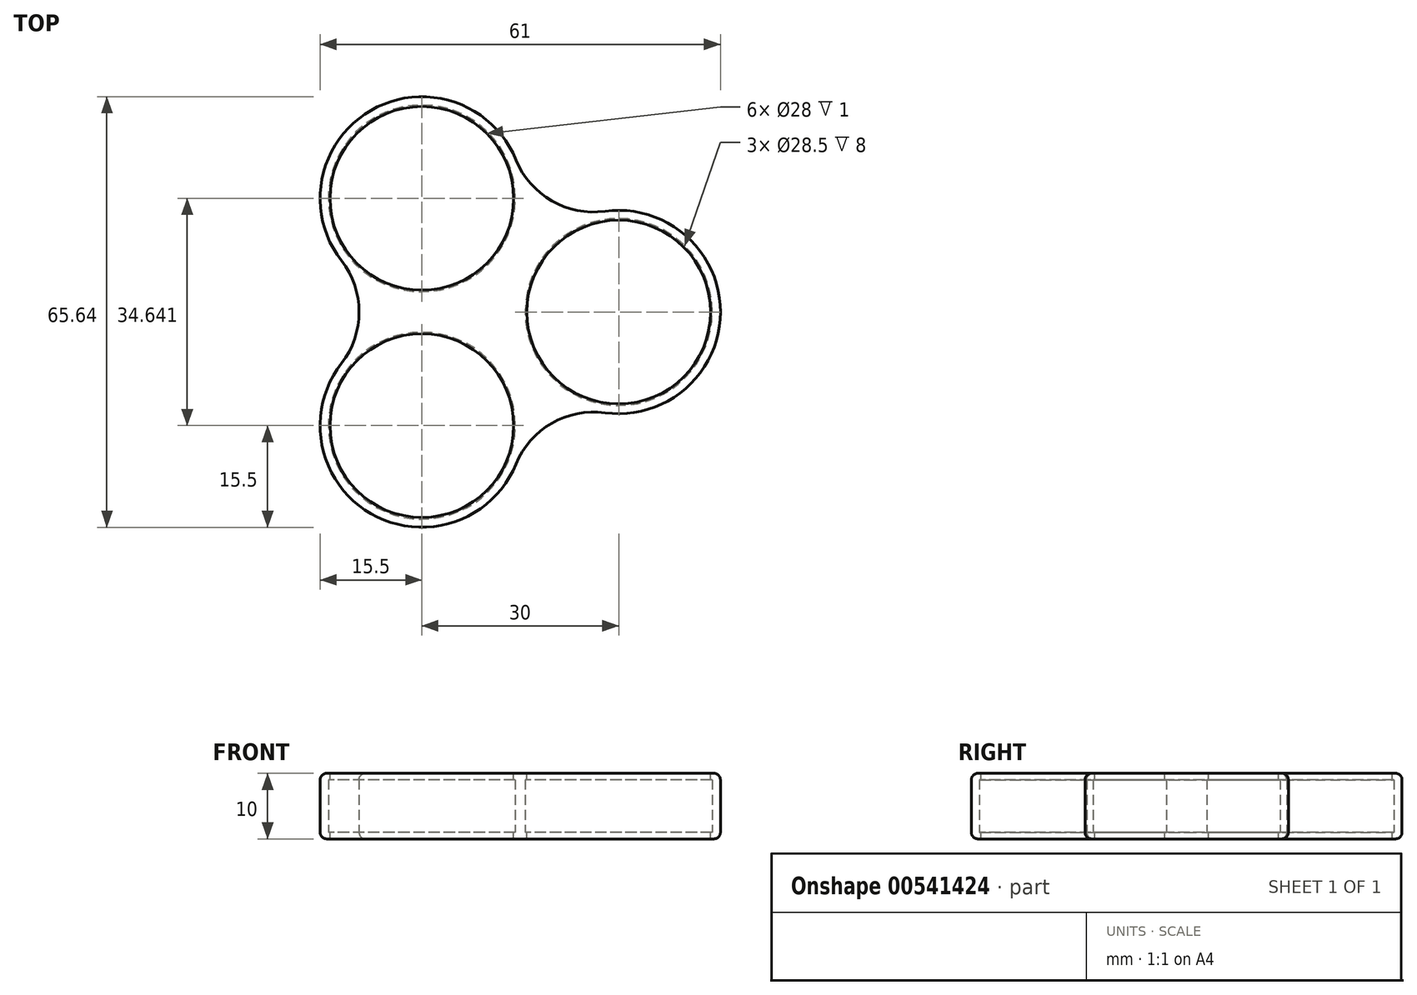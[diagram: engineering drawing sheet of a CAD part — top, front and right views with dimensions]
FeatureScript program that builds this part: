
annotation { "Feature Type Name" : "Feature", "Feature Type Description" : "" }
export const myFeature = defineFeature(function(context is Context, id is Id, definition is map)
    precondition{}
    {
        {
            var Q0;
            Q0=qCreatedBy(makeId("Top.planeOp"),FACE);
            var sketch = newSketch(context, id + "F0", { "sketchPlane" : qUnion([Q0])});
            skCircle(sketch, "E0", {"center": v(20, 0) * mm, "radius": 15.5 * mm});
            skCircle(sketch, "E1.1.0", {"center": v(-10, 17.32) * mm, "radius": 15.5 * mm});
            skCircle(sketch, "E1.2.0", {"center": v(-10, -17.32) * mm, "radius": 15.5 * mm});
            skPoint(sketch, "E1.center", {"position": v(0, 0) * mm});
            skCircle(sketch, "E2", {"center": v(16.18, 28.03) * mm, "radius": 12.79 * mm});
            skCircle(sketch, "E3.1.0", {"center": v(-32.36, 0) * mm, "radius": 12.79 * mm});
            skCircle(sketch, "E3.2.0", {"center": v(16.18, -28.03) * mm, "radius": 12.79 * mm});
            skSolve(sketch);
        }
        {
            var Q0;
            {var subQ0=sQuery(id+"F0.wireOp",EDGE,"E2");var subQ1=sQuery(id+"F0.wireOp",EDGE,"E0");var subQ2=makeQuery(id+"F0.imprint","INTERSECT",VERTEX,{"disambiguationData":[OD(0.0)],"derivedFrom":[subQ1,subQ0]});Q0=makeQuery(id+"F0.imprint","IMPRINT",FACE,{"disambiguationData":[TD([[makeQuery(id+"F0.imprint","IMPRINT",EDGE,{"disambiguationData":[TD([[subQ2,-1.0]])],"derivedFrom":subQ1}),1.0]])]});}
            var Q1;
            {var subQ0=sQuery(id+"F0.wireOp",EDGE,"E0");var subQ1=makeQuery(id+"F0.imprint","INTERSECT",VERTEX,{"derivedFrom":[subQ0,sQuery(id+"F0.wireOp",EDGE,"E3.2.0")]});Q1=makeQuery(id+"F0.imprint","IMPRINT",FACE,{"disambiguationData":[TD([[makeQuery(id+"F0.imprint","IMPRINT",EDGE,{"disambiguationData":[TD([[subQ1,1.0]])],"derivedFrom":subQ0}),1.0]])]});}
            var Q2;
            {var subQ0=sQuery(id+"F0.wireOp",EDGE,"E3.1.0");var subQ1=sQuery(id+"F0.wireOp",EDGE,"E1.1.0");var subQ2=makeQuery(id+"F0.imprint","INTERSECT",VERTEX,{"disambiguationData":[OD(0.0)],"derivedFrom":[subQ1,subQ0]});Q2=makeQuery(id+"F0.imprint","IMPRINT",FACE,{"disambiguationData":[TD([[makeQuery(id+"F0.imprint","IMPRINT",EDGE,{"disambiguationData":[TD([[subQ2,-1.0]])],"derivedFrom":subQ1}),1.0]])]});}
            var Q3;
            {var subQ0=sQuery(id+"F0.wireOp",EDGE,"E3.2.0");var subQ1=sQuery(id+"F0.wireOp",EDGE,"E1.2.0");var subQ2=makeQuery(id+"F0.imprint","INTERSECT",VERTEX,{"disambiguationData":[OD(0.0)],"derivedFrom":[subQ1,subQ0]});Q3=makeQuery(id+"F0.imprint","IMPRINT",FACE,{"disambiguationData":[TD([[makeQuery(id+"F0.imprint","IMPRINT",EDGE,{"disambiguationData":[TD([[subQ2,-1.0]])],"derivedFrom":subQ1}),1.0]])]});}
            var Q4;
            {var subQ0=sQuery(id+"F0.wireOp",EDGE,"E1.2.0");var subQ1=makeQuery(id+"F0.imprint","INTERSECT",VERTEX,{"derivedFrom":[subQ0,sQuery(id+"F0.wireOp",EDGE,"E3.1.0")]});Q4=makeQuery(id+"F0.imprint","IMPRINT",FACE,{"disambiguationData":[TD([[makeQuery(id+"F0.imprint","IMPRINT",EDGE,{"disambiguationData":[TD([[subQ1,1.0]])],"derivedFrom":subQ0}),1.0]])]});}
            var Q5;
            {var subQ3=sQuery(id+"F0.wireOp",EDGE,"E3.2.0");var subQ8=sQuery(id+"F0.wireOp",EDGE,"E0");var subQ11=makeQuery(id+"F0.imprint","INTERSECT",VERTEX,{"derivedFrom":[subQ8,subQ3]});Q5=makeQuery(id+"F0.imprint","IMPRINT",FACE,{"disambiguationData":[TD([[makeQuery(id+"F0.imprint","IMPRINT",EDGE,{"disambiguationData":[TD([[subQ11,1.0]])],"derivedFrom":subQ8}),-1.0]])]});}
            var Q6;
            {var subQ0=sQuery(id+"F0.wireOp",EDGE,"E1.1.0");var subQ1=makeQuery(id+"F0.imprint","INTERSECT",VERTEX,{"derivedFrom":[subQ0,sQuery(id+"F0.wireOp",EDGE,"E2")]});Q6=makeQuery(id+"F0.imprint","IMPRINT",FACE,{"disambiguationData":[TD([[makeQuery(id+"F0.imprint","IMPRINT",EDGE,{"disambiguationData":[TD([[subQ1,1.0]])],"derivedFrom":subQ0}),1.0]])]});}
            extrude(context, id + "F1", {"entities" : qUnion([Q0, Q1, Q2, Q3, Q4, Q5, Q6]), "depth" : 10 * mm, "offsetDistance" : 25 * mm});
        }
        {
            var Q0;
            Q0=qCreatedBy(makeId("Top.planeOp"),FACE);
            var sketch = newSketch(context, id + "F2", { "sketchPlane" : qUnion([Q0])});
            skCircle(sketch, "E4", {"center": v(20, 0) * mm, "radius": 14 * mm});
            skCircle(sketch, "E5.1.0", {"center": v(-10, 17.32) * mm, "radius": 14 * mm});
            skCircle(sketch, "E5.2.0", {"center": v(-10, -17.32) * mm, "radius": 14 * mm});
            skPoint(sketch, "E5.center", {"position": v(0, 0) * mm});
            skSolve(sketch);
        }
        {
            var Q0;
            Q0 = qSketchRegion(id + "F2", true);
            extrude(context, id + "F3", {"entities" : qUnion([Q0]), "operationType" : NewBodyOperationType.REMOVE, "oppositeDirection" : true, "depth" : 25 * mm, "offsetDistance" : 25 * mm, "hasSecondDirection" : true, "secondDirectionOppositeDirection" : true, "secondDirectionDepth" : -25 * mm});
        }
        {
            var Q0;
            Q0=qCreatedBy(makeId("Top.planeOp"),FACE);
            var sketch = newSketch(context, id + "F4", { "sketchPlane" : qUnion([Q0])});
            skCircle(sketch, "E6", {"center": v(20, 0) * mm, "radius": 14.25 * mm});
            skCircle(sketch, "E7.1.0", {"center": v(-10, 17.32) * mm, "radius": 14.25 * mm});
            skCircle(sketch, "E7.2.0", {"center": v(-10, -17.32) * mm, "radius": 14.25 * mm});
            skPoint(sketch, "E7.center", {"position": v(0, 0) * mm});
            skSolve(sketch);
        }
        {
            var Q0;
            Q0 = qSketchRegion(id + "F4", true);
            extrude(context, id + "F5", {"entities" : qUnion([Q0]), "operationType" : NewBodyOperationType.REMOVE, "depth" : 9 * mm, "offsetDistance" : 25 * mm, "hasSecondDirection" : true, "secondDirectionOppositeDirection" : true, "secondDirectionDepth" : -1 * mm});
        }
        {
            var Q0;
            Q0=makeQuery(id+"F1.opExtrude","CAP_EDGE",EDGE,{"disambiguationData":[OSD([sQuery(id+"F0.wireOp",EDGE,"E1.2.0")])],"isStart":false});
            var Q1;
            Q1=makeQuery(id+"F1.opExtrude","CAP_EDGE",EDGE,{"disambiguationData":[OSD([sQuery(id+"F0.wireOp",EDGE,"E3.2.0")])],"isStart":false});
            var Q2;
            Q2=makeQuery(id+"F1.opExtrude","CAP_EDGE",EDGE,{"disambiguationData":[OSD([sQuery(id+"F0.wireOp",EDGE,"E0")])],"isStart":false});
            var Q3;
            Q3=makeQuery(id+"F1.opExtrude","CAP_EDGE",EDGE,{"disambiguationData":[OSD([sQuery(id+"F0.wireOp",EDGE,"E2")])],"isStart":false});
            var Q4;
            Q4=makeQuery(id+"F1.opExtrude","CAP_EDGE",EDGE,{"disambiguationData":[OSD([sQuery(id+"F0.wireOp",EDGE,"E3.1.0")])],"isStart":false});
            var Q5;
            Q5=makeQuery(id+"F1.opExtrude","CAP_EDGE",EDGE,{"disambiguationData":[OSD([sQuery(id+"F0.wireOp",EDGE,"E1.1.0")])],"isStart":false});
            fillet(context, id + "F6", {"entities" : qUnion([Q0, Q1, Q2, Q3, Q4, Q5]), "radius" : 1 * mm, "tangentPropagation" : true, "allowEdgeOverflow" : false});
        }
        {
            var Q0;
            Q0=makeQuery(id+"F1.opExtrude","CAP_EDGE",EDGE,{"disambiguationData":[OSD([sQuery(id+"F0.wireOp",EDGE,"E1.1.0")])],"isStart":true});
            var Q1;
            Q1=makeQuery(id+"F1.opExtrude","CAP_EDGE",EDGE,{"disambiguationData":[OSD([sQuery(id+"F0.wireOp",EDGE,"E2")])],"isStart":true});
            var Q2;
            Q2=makeQuery(id+"F1.opExtrude","CAP_EDGE",EDGE,{"disambiguationData":[OSD([sQuery(id+"F0.wireOp",EDGE,"E0")])],"isStart":true});
            var Q3;
            Q3=makeQuery(id+"F1.opExtrude","CAP_EDGE",EDGE,{"disambiguationData":[OSD([sQuery(id+"F0.wireOp",EDGE,"E3.2.0")])],"isStart":true});
            var Q4;
            Q4=makeQuery(id+"F1.opExtrude","CAP_EDGE",EDGE,{"disambiguationData":[OSD([sQuery(id+"F0.wireOp",EDGE,"E1.2.0")])],"isStart":true});
            var Q5;
            Q5=makeQuery(id+"F1.opExtrude","CAP_EDGE",EDGE,{"disambiguationData":[OSD([sQuery(id+"F0.wireOp",EDGE,"E3.1.0")])],"isStart":true});
            fillet(context, id + "F7", {"entities" : qUnion([Q0, Q1, Q2, Q3, Q4, Q5]), "radius" : 1 * mm, "tangentPropagation" : true, "allowEdgeOverflow" : false});
        }
    });
